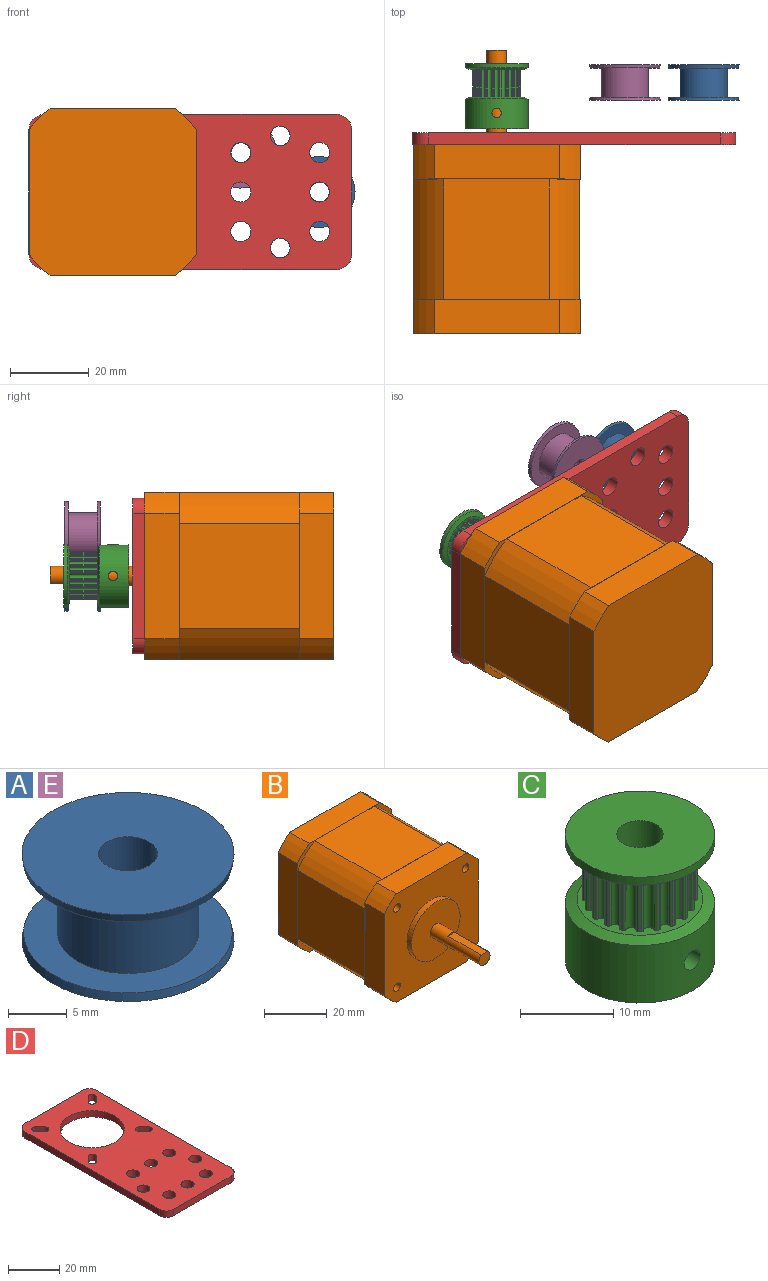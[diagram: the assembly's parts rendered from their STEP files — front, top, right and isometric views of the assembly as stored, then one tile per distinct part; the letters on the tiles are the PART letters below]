
ASSEMBLY  parts=5 mates=6
PART A: 8 faces, bbox 18x18x9 mm
  f0: plane 17.72x17.72mm, normal (0,0,-1), area 133.5mm2, adj f1,f6
  f1: cylinder r=6mm len=12mm, axis (0,0,-1), area 279mm2, adj f0,f2
  f2: plane 17.72x17.72mm, normal (0,0,1), area 133.5mm2, adj f1,f3
  f3: cone r=9mm half-angle=10deg, axis (0,0,-1), area 45.6mm2, adj f2,f4
  f4: plane 18x18mm, normal (0,0,-1), area 234.8mm2, adj f3,f7
  f5: plane 18x18mm, normal (0,0,1), area 234.8mm2, adj f6,f7
  f6: cone r=8.86mm half-angle=10deg, axis (0,0,1), area 45.6mm2, adj f0,f5
  f7: cylinder r=2.5mm len=9mm, axis (0,0,1), area 141.4mm2, adj f4,f5
PART B: 50 faces, bbox 42.4x72x42.4 mm
  f0: cylinder r=2.5mm len=22mm, axis (0,1,0), area 297.3mm2, adj f1,f2,f29,f30
  f1: plane 5x4.5mm, normal (0,-1,0), area 18.6mm2, adj f0,f29
  f2: plane 22x22mm, normal (0,-1,0), area 360.5mm2, adj f0,f3
  f3: cylinder r=11mm len=22mm, axis (0,1,0), area 138.2mm2, adj f2,f8
  f4: plane 31.78x8.75mm, normal (1,0,0), area 278mm2, adj f8,f9,f10,f32
  f5: plane 31.78x8.75mm, normal (0,0,-1), area 278mm2, adj f8,f9,f11,f32
  f6: plane 31.78x8.75mm, normal (-1,0,0), area 278mm2, adj f8,f11,f12,f32
  f7: plane 31.78x8.75mm, normal (0,0,1), area 278mm2, adj f8,f10,f12,f32
  f8: plane 42.42x42.42mm, normal (0,-1,0), area 1339.6mm2, adj f3,f4,f5,f6,f7,f9,f10,f11
  f9: cylinder r=26.5mm len=8.75mm, axis (0,1,0), area 66.1mm2, adj f4,f5,f8,f32
  f10: cylinder r=26.5mm len=8.75mm, axis (0,1,0), area 66.1mm2, adj f4,f7,f8,f32
  f11: cylinder r=26.5mm len=8.75mm, axis (0,1,0), area 66.1mm2, adj f5,f6,f8,f32
  f12: cylinder r=26.5mm len=8.75mm, axis (0,1,0), area 66.1mm2, adj f6,f7,f8,f32
  f13: cone r=1.25mm half-angle=59deg, axis (0,-1,0), area 5.7mm2, adj f14
  f14: cylinder r=1.25mm len=2.5mm, axis (0,-1,0), area 11.8mm2, adj f13,f15
  f15: plane 3x3mm, normal (0,-1,0), area 2.2mm2, adj f14,f16
  f16: cylinder r=1.5mm len=6mm, axis (0,-1,0), area 56.5mm2, adj f8,f15
  f17: cone r=1.25mm half-angle=59deg, axis (0,-1,0), area 5.7mm2, adj f18
  f18: cylinder r=1.25mm len=2.5mm, axis (0,-1,0), area 11.8mm2, adj f17,f19
  f19: plane 3x3mm, normal (0,-1,0), area 2.2mm2, adj f18,f20
  f20: cylinder r=1.5mm len=6mm, axis (0,-1,0), area 56.5mm2, adj f8,f19
  f21: cone r=1.25mm half-angle=59deg, axis (0,-1,0), area 5.7mm2, adj f22
  f22: cylinder r=1.25mm len=2.5mm, axis (0,-1,0), area 11.8mm2, adj f21,f23
  f23: plane 3x3mm, normal (0,-1,0), area 2.2mm2, adj f22,f24
  f24: cylinder r=1.5mm len=6mm, axis (0,-1,0), area 56.5mm2, adj f8,f23
  f25: cone r=1.25mm half-angle=59deg, axis (0,-1,0), area 5.7mm2, adj f26
  f26: cylinder r=1.25mm len=2.5mm, axis (0,-1,0), area 11.8mm2, adj f25,f27
  f27: plane 3x3mm, normal (0,-1,0), area 2.2mm2, adj f26,f28
  f28: cylinder r=1.5mm len=6mm, axis (0,-1,0), area 56.5mm2, adj f8,f27
  f29: plane 15x3mm, normal (0,0,1), area 45mm2, adj f0,f1,f30
  f30: plane 3x0.5mm, normal (0,-1,0), area 1mm2, adj f0,f29
  f31: plane 42.42x42.42mm, normal (0,-1,0), area 67.2mm2, adj f33,f34,f35,f36,f37,f38,f39,f40
  f32: plane 42.42x42.42mm, normal (0,1,0), area 67.2mm2, adj f4,f5,f6,f7,f9,f10,f11,f12
  f33: cylinder r=25mm len=30.5mm, axis (0,-1,0), area 335.5mm2, adj f31,f32,f34,f40
  f34: plane 30.5x26.79mm, normal (0,0,1), area 817.1mm2, adj f31,f32,f33,f35
  f35: cylinder r=25mm len=30.5mm, axis (0,-1,0), area 335.5mm2, adj f31,f32,f34,f36
  f36: plane 30.5x26.79mm, normal (1,0,0), area 817.1mm2, adj f31,f32,f35,f37
  f37: cylinder r=25mm len=30.5mm, axis (0,-1,0), area 335.5mm2, adj f31,f32,f36,f38
  f38: plane 30.5x26.79mm, normal (0,0,-1), area 817.1mm2, adj f31,f32,f37,f39
  f39: cylinder r=25mm len=30.5mm, axis (0,-1,0), area 335.5mm2, adj f31,f32,f38,f40
  f40: plane 30.5x26.79mm, normal (-1,0,0), area 817.1mm2, adj f31,f32,f33,f39
  f41: plane 42.42x42.42mm, normal (0,1,0), area 1748.1mm2, adj f42,f43,f44,f45,f46,f47,f48,f49
  f42: cylinder r=26.5mm len=8.75mm, axis (0,1,0), area 66.1mm2, adj f31,f41,f48,f49
  f43: cylinder r=26.5mm len=8.75mm, axis (0,1,0), area 66.1mm2, adj f31,f41,f47,f48
  f44: cylinder r=26.5mm len=8.75mm, axis (0,1,0), area 66.1mm2, adj f31,f41,f46,f47
  f45: cylinder r=26.5mm len=8.75mm, axis (0,1,0), area 66.1mm2, adj f31,f41,f46,f49
  f46: plane 31.78x8.75mm, normal (0,0,1), area 278mm2, adj f31,f41,f44,f45
  f47: plane 31.78x8.75mm, normal (-1,0,0), area 278mm2, adj f31,f41,f43,f44
  f48: plane 31.78x8.75mm, normal (0,0,-1), area 278mm2, adj f31,f41,f42,f43
  f49: plane 31.78x8.75mm, normal (1,0,0), area 278mm2, adj f31,f41,f42,f45
PART C: 131 faces, bbox 16x16x16.5 mm
  f0: cylinder r=8mm len=16mm, axis (0,0,-1), area 370mm2, adj f123,f124,f129,f130
  f1: cylinder r=2.5mm len=16.5mm, axis (0,0,-1), area 249.8mm2, adj f123,f126,f129,f130
  f2: cylinder r=6.11mm len=7mm, axis (0,0,-1), area 2.2mm2, adj f3,f14,f122,f125
  f3: cylinder r=0.19mm len=7mm, axis (0,0,-1), area 1.8mm2, adj f2,f4,f122,f125
  f4: cylinder r=5mm len=7mm, axis (0,0,-1), area 1.6mm2, adj f3,f5,f122,f125
  f5: cylinder r=0.56mm len=7mm, axis (0,0,-1), area 9.4mm2, adj f4,f6,f122,f125
  f6: cylinder r=5mm len=7mm, axis (0,0,-1), area 1.6mm2, adj f5,f7,f122,f125
  f7: cylinder r=0.19mm len=7mm, axis (0,0,-1), area 1.8mm2, adj f6,f8,f122,f125
  f8: cylinder r=6.11mm len=7mm, axis (0,0,-1), area 2.2mm2, adj f7,f117,f122,f125
  f9: cylinder r=6.11mm len=7mm, axis (0,0,-1), area 2.2mm2, adj f10,f20,f122,f125
  f10: cylinder r=0.19mm len=7mm, axis (0,0,-1), area 1.8mm2, adj f9,f11,f122,f125
  f11: cylinder r=5mm len=7mm, axis (0,0,-1), area 1.6mm2, adj f10,f12,f122,f125
  f12: cylinder r=0.56mm len=7mm, axis (0,0,-1), area 9.4mm2, adj f11,f13,f122,f125
  f13: cylinder r=5mm len=7mm, axis (0,0,-1), area 1.6mm2, adj f12,f14,f122,f125
  f14: cylinder r=0.19mm len=7mm, axis (0,0,-1), area 1.8mm2, adj f2,f13,f122,f125
  f15: cylinder r=6.11mm len=7mm, axis (0,0,-1), area 2.2mm2, adj f16,f26,f122,f125
  f16: cylinder r=0.19mm len=7mm, axis (0,0,-1), area 1.8mm2, adj f15,f17,f122,f125
  f17: cylinder r=5mm len=7mm, axis (0,0,-1), area 1.6mm2, adj f16,f18,f122,f125
  f18: cylinder r=0.56mm len=7mm, axis (0,0,-1), area 9.4mm2, adj f17,f19,f122,f125
  f19: cylinder r=5mm len=7mm, axis (0,0,-1), area 1.6mm2, adj f18,f20,f122,f125
  f20: cylinder r=0.19mm len=7mm, axis (0,0,-1), area 1.8mm2, adj f9,f19,f122,f125
  f21: cylinder r=6.11mm len=7mm, axis (0,0,-1), area 2.2mm2, adj f22,f32,f122,f125
  f22: cylinder r=0.19mm len=7mm, axis (0,0,-1), area 1.8mm2, adj f21,f23,f122,f125
  f23: cylinder r=5mm len=7mm, axis (0,0,-1), area 1.6mm2, adj f22,f24,f122,f125
  f24: cylinder r=0.56mm len=7mm, axis (0,0,-1), area 9.4mm2, adj f23,f25,f122,f125
  f25: cylinder r=5mm len=7mm, axis (0,0,-1), area 1.6mm2, adj f24,f26,f122,f125
  f26: cylinder r=0.19mm len=7mm, axis (0,0,-1), area 1.8mm2, adj f15,f25,f122,f125
  f27: cylinder r=6.11mm len=7mm, axis (0,0,-1), area 2.2mm2, adj f28,f38,f122,f125
  f28: cylinder r=0.19mm len=7mm, axis (0,0,-1), area 1.8mm2, adj f27,f29,f122,f125
  f29: cylinder r=5mm len=7mm, axis (0,0,-1), area 1.6mm2, adj f28,f30,f122,f125
  f30: cylinder r=0.56mm len=7mm, axis (0,0,-1), area 9.4mm2, adj f29,f31,f122,f125
  f31: cylinder r=5mm len=7mm, axis (0,0,-1), area 1.6mm2, adj f30,f32,f122,f125
  f32: cylinder r=0.19mm len=7mm, axis (0,0,-1), area 1.8mm2, adj f21,f31,f122,f125
  f33: cylinder r=6.11mm len=7mm, axis (0,0,-1), area 2.2mm2, adj f34,f44,f122,f125
  f34: cylinder r=0.19mm len=7mm, axis (0,0,-1), area 1.8mm2, adj f33,f35,f122,f125
  f35: cylinder r=5mm len=7mm, axis (0,0,-1), area 1.6mm2, adj f34,f36,f122,f125
  f36: cylinder r=0.56mm len=7mm, axis (0,0,-1), area 9.4mm2, adj f35,f37,f122,f125
  f37: cylinder r=5mm len=7mm, axis (0,0,-1), area 1.6mm2, adj f36,f38,f122,f125
  f38: cylinder r=0.19mm len=7mm, axis (0,0,-1), area 1.8mm2, adj f27,f37,f122,f125
  f39: cylinder r=6.11mm len=7mm, axis (0,0,-1), area 2.2mm2, adj f40,f50,f122,f125
  f40: cylinder r=0.19mm len=7mm, axis (0,0,-1), area 1.8mm2, adj f39,f41,f122,f125
  f41: cylinder r=5mm len=7mm, axis (0,0,-1), area 1.6mm2, adj f40,f42,f122,f125
  f42: cylinder r=0.56mm len=7mm, axis (0,0,-1), area 9.4mm2, adj f41,f43,f122,f125
  f43: cylinder r=5mm len=7mm, axis (0,0,-1), area 1.6mm2, adj f42,f44,f122,f125
  f44: cylinder r=0.19mm len=7mm, axis (0,0,-1), area 1.8mm2, adj f33,f43,f122,f125
  f45: cylinder r=6.11mm len=7mm, axis (0,0,-1), area 2.2mm2, adj f46,f56,f122,f125
  f46: cylinder r=0.19mm len=7mm, axis (0,0,-1), area 1.8mm2, adj f45,f47,f122,f125
  f47: cylinder r=5mm len=7mm, axis (0,0,-1), area 1.6mm2, adj f46,f48,f122,f125
  f48: cylinder r=0.56mm len=7mm, axis (0,0,-1), area 9.4mm2, adj f47,f49,f122,f125
  f49: cylinder r=5mm len=7mm, axis (0,0,-1), area 1.6mm2, adj f48,f50,f122,f125
  f50: cylinder r=0.19mm len=7mm, axis (0,0,-1), area 1.8mm2, adj f39,f49,f122,f125
  f51: cylinder r=6.11mm len=7mm, axis (0,0,-1), area 2.2mm2, adj f52,f62,f122,f125
  f52: cylinder r=0.19mm len=7mm, axis (0,0,-1), area 1.8mm2, adj f51,f53,f122,f125
  f53: cylinder r=5mm len=7mm, axis (0,0,-1), area 1.6mm2, adj f52,f54,f122,f125
  f54: cylinder r=0.56mm len=7mm, axis (0,0,-1), area 9.4mm2, adj f53,f55,f122,f125
  f55: cylinder r=5mm len=7mm, axis (0,0,-1), area 1.6mm2, adj f54,f56,f122,f125
  f56: cylinder r=0.19mm len=7mm, axis (0,0,-1), area 1.8mm2, adj f45,f55,f122,f125
  f57: cylinder r=6.11mm len=7mm, axis (0,0,-1), area 2.2mm2, adj f58,f68,f122,f125
  f58: cylinder r=0.19mm len=7mm, axis (0,0,-1), area 1.8mm2, adj f57,f59,f122,f125
  f59: cylinder r=5mm len=7mm, axis (0,0,-1), area 1.6mm2, adj f58,f60,f122,f125
  f60: cylinder r=0.56mm len=7mm, axis (0,0,-1), area 9.4mm2, adj f59,f61,f122,f125
  f61: cylinder r=5mm len=7mm, axis (0,0,-1), area 1.6mm2, adj f60,f62,f122,f125
  f62: cylinder r=0.19mm len=7mm, axis (0,0,-1), area 1.8mm2, adj f51,f61,f122,f125
  f63: cylinder r=6.11mm len=7mm, axis (0,0,-1), area 2.2mm2, adj f64,f74,f122,f125
  f64: cylinder r=0.19mm len=7mm, axis (0,0,-1), area 1.8mm2, adj f63,f65,f122,f125
  f65: cylinder r=5mm len=7mm, axis (0,0,-1), area 1.6mm2, adj f64,f66,f122,f125
  f66: cylinder r=0.56mm len=7mm, axis (0,0,-1), area 9.4mm2, adj f65,f67,f122,f125
  f67: cylinder r=5mm len=7mm, axis (0,0,-1), area 1.6mm2, adj f66,f68,f122,f125
  f68: cylinder r=0.19mm len=7mm, axis (0,0,-1), area 1.8mm2, adj f57,f67,f122,f125
  f69: cylinder r=6.11mm len=7mm, axis (0,0,-1), area 2.2mm2, adj f70,f80,f122,f125
  f70: cylinder r=0.19mm len=7mm, axis (0,0,-1), area 1.8mm2, adj f69,f71,f122,f125
  f71: cylinder r=5mm len=7mm, axis (0,0,-1), area 1.6mm2, adj f70,f72,f122,f125
  f72: cylinder r=0.56mm len=7mm, axis (0,0,-1), area 9.4mm2, adj f71,f73,f122,f125
  f73: cylinder r=5mm len=7mm, axis (0,0,-1), area 1.6mm2, adj f72,f74,f122,f125
  f74: cylinder r=0.19mm len=7mm, axis (0,0,-1), area 1.8mm2, adj f63,f73,f122,f125
  f75: cylinder r=6.11mm len=7mm, axis (0,0,-1), area 2.2mm2, adj f76,f86,f122,f125
  f76: cylinder r=0.19mm len=7mm, axis (0,0,-1), area 1.8mm2, adj f75,f77,f122,f125
  f77: cylinder r=5mm len=7mm, axis (0,0,-1), area 1.6mm2, adj f76,f78,f122,f125
  f78: cylinder r=0.56mm len=7mm, axis (0,0,-1), area 9.4mm2, adj f77,f79,f122,f125
  f79: cylinder r=5mm len=7mm, axis (0,0,-1), area 1.6mm2, adj f78,f80,f122,f125
  f80: cylinder r=0.19mm len=7mm, axis (0,0,-1), area 1.8mm2, adj f69,f79,f122,f125
  f81: cylinder r=6.11mm len=7mm, axis (0,0,-1), area 2.2mm2, adj f82,f92,f122,f125
  f82: cylinder r=0.19mm len=7mm, axis (0,0,-1), area 1.8mm2, adj f81,f83,f122,f125
  f83: cylinder r=5mm len=7mm, axis (0,0,-1), area 1.6mm2, adj f82,f84,f122,f125
  f84: cylinder r=0.56mm len=7mm, axis (0,0,-1), area 9.4mm2, adj f83,f85,f122,f125
  f85: cylinder r=5mm len=7mm, axis (0,0,-1), area 1.6mm2, adj f84,f86,f122,f125
  f86: cylinder r=0.19mm len=7mm, axis (0,0,-1), area 1.8mm2, adj f75,f85,f122,f125
  f87: cylinder r=6.11mm len=7mm, axis (0,0,-1), area 2.2mm2, adj f88,f98,f122,f125
  f88: cylinder r=0.19mm len=7mm, axis (0,0,-1), area 1.8mm2, adj f87,f89,f122,f125
  f89: cylinder r=5mm len=7mm, axis (0,0,-1), area 1.6mm2, adj f88,f90,f122,f125
  f90: cylinder r=0.56mm len=7mm, axis (0,0,-1), area 9.4mm2, adj f89,f91,f122,f125
  f91: cylinder r=5mm len=7mm, axis (0,0,-1), area 1.6mm2, adj f90,f92,f122,f125
  f92: cylinder r=0.19mm len=7mm, axis (0,0,-1), area 1.8mm2, adj f81,f91,f122,f125
  f93: cylinder r=6.11mm len=7mm, axis (0,0,-1), area 2.2mm2, adj f94,f104,f122,f125
  f94: cylinder r=0.19mm len=7mm, axis (0,0,-1), area 1.8mm2, adj f93,f95,f122,f125
  f95: cylinder r=5mm len=7mm, axis (0,0,-1), area 1.6mm2, adj f94,f96,f122,f125
  f96: cylinder r=0.56mm len=7mm, axis (0,0,-1), area 9.4mm2, adj f95,f97,f122,f125
  f97: cylinder r=5mm len=7mm, axis (0,0,-1), area 1.6mm2, adj f96,f98,f122,f125
  f98: cylinder r=0.19mm len=7mm, axis (0,0,-1), area 1.8mm2, adj f87,f97,f122,f125
  f99: cylinder r=6.11mm len=7mm, axis (0,0,-1), area 2.2mm2, adj f100,f110,f122,f125
  f100: cylinder r=0.19mm len=7mm, axis (0,0,-1), area 1.8mm2, adj f99,f101,f122,f125
  f101: cylinder r=5mm len=7mm, axis (0,0,-1), area 1.6mm2, adj f100,f102,f122,f125
  f102: cylinder r=0.56mm len=7mm, axis (0,0,-1), area 9.4mm2, adj f101,f103,f122,f125
  f103: cylinder r=5mm len=7mm, axis (0,0,-1), area 1.6mm2, adj f102,f104,f122,f125
  f104: cylinder r=0.19mm len=7mm, axis (0,0,-1), area 1.8mm2, adj f93,f103,f122,f125
  f105: cylinder r=6.11mm len=7mm, axis (0,0,-1), area 2.2mm2, adj f106,f116,f122,f125
  f106: cylinder r=0.19mm len=7mm, axis (0,0,-1), area 1.8mm2, adj f105,f107,f122,f125
  f107: cylinder r=5mm len=7mm, axis (0,0,-1), area 1.6mm2, adj f106,f108,f122,f125
  f108: cylinder r=0.56mm len=7mm, axis (0,0,-1), area 9.4mm2, adj f107,f109,f122,f125
  f109: cylinder r=5mm len=7mm, axis (0,0,-1), area 1.6mm2, adj f108,f110,f122,f125
  f110: cylinder r=0.19mm len=7mm, axis (0,0,-1), area 1.8mm2, adj f99,f109,f122,f125
  f111: cylinder r=6.11mm len=7mm, axis (0,0,-1), area 2.2mm2, adj f112,f121,f122,f125
  f112: cylinder r=0.19mm len=7mm, axis (0,0,-1), area 1.8mm2, adj f111,f113,f122,f125
  f113: cylinder r=5mm len=7mm, axis (0,0,-1), area 1.6mm2, adj f112,f114,f122,f125
  f114: cylinder r=0.56mm len=7mm, axis (0,0,-1), area 9.4mm2, adj f113,f115,f122,f125
  f115: cylinder r=5mm len=7mm, axis (0,0,-1), area 1.6mm2, adj f114,f116,f122,f125
  f116: cylinder r=0.19mm len=7mm, axis (0,0,-1), area 1.8mm2, adj f105,f115,f122,f125
  f117: cylinder r=0.19mm len=7mm, axis (0,0,-1), area 1.8mm2, adj f8,f118,f122,f125
  f118: cylinder r=5mm len=7mm, axis (0,0,-1), area 1.6mm2, adj f117,f119,f122,f125
  f119: cylinder r=0.56mm len=7mm, axis (0,0,-1), area 9.4mm2, adj f118,f120,f122,f125
  f120: cylinder r=5mm len=7mm, axis (0,0,-1), area 1.6mm2, adj f119,f121,f122,f125
  f121: cylinder r=0.19mm len=7mm, axis (0,0,-1), area 1.8mm2, adj f111,f120,f122,f125
  f122: plane 13.48x13.48mm, normal (0,0,1), area 40mm2, adj f2,f3,f4,f5,f6,f7,f8,f9
  f123: plane 16x16mm, normal (0,0,-1), area 181.4mm2, adj f0,f1
  f124: cone r=6.74mm half-angle=70deg, axis (0,0,-1), area 62mm2, adj f0,f122
  f125: plane 13.48x13.48mm, normal (0,0,-1), area 40mm2, adj f2,f3,f4,f5,f6,f7,f8,f9
  f126: plane 16x16mm, normal (0,0,1), area 181.4mm2, adj f1,f128
  f127: cone r=8mm half-angle=70deg, axis (0,0,1), area 62mm2, adj f125,f128
  f128: cylinder r=8mm len=16mm, axis (0,0,-1), area 52.4mm2, adj f126,f127
  f129: cylinder r=1.2mm len=5.81mm, axis (0,1,0), area 42.3mm2, adj f0,f1
  f130: cylinder r=1.2mm len=5.81mm, axis (-1,0,0), area 42.3mm2, adj f0,f1
PART D: 35 faces, bbox 39.5x82x3 mm
  f0: plane 82x39.5mm, normal (0,0,1), area 2498.5mm2, adj f2,f3,f4,f5,f6,f7,f8,f9
  f1: plane 82x39.5mm, normal (0,0,-1), area 2498.5mm2, adj f2,f3,f4,f5,f6,f7,f8,f9
  f2: cylinder r=4mm len=4mm, axis (0,0,-1), area 18.8mm2, adj f0,f1,f3,f9
  f3: plane 31.5x3mm, normal (0,-1,0), area 94.5mm2, adj f0,f1,f2,f4
  f4: cylinder r=4mm len=4mm, axis (0,0,-1), area 18.8mm2, adj f0,f1,f3,f5
  f5: plane 74x3mm, normal (1,0,0), area 222mm2, adj f0,f1,f4,f6
  f6: cylinder r=4mm len=4mm, axis (0,0,-1), area 18.8mm2, adj f0,f1,f5,f7
  f7: plane 31.5x3mm, normal (0,1,0), area 94.5mm2, adj f0,f1,f6,f8
  f8: cylinder r=4mm len=4mm, axis (0,0,-1), area 18.8mm2, adj f0,f1,f7,f9
  f9: plane 74x3mm, normal (-1,0,0), area 222mm2, adj f0,f1,f2,f8
  f10: cylinder r=12.5mm len=25mm, axis (0,0,-1), area 235.6mm2, adj f0,f1
  f11: cylinder r=1.55mm len=3mm, axis (0,0,-1), area 14.6mm2, adj f0,f1,f12,f14
  f12: plane 3x2.5mm, normal (-0.71,0.71,0), area 10.6mm2, adj f0,f1,f11,f13
  f13: cylinder r=1.55mm len=3mm, axis (0,0,-1), area 14.6mm2, adj f0,f1,f12,f14
  f14: plane 3x2.5mm, normal (0.71,-0.71,0), area 10.6mm2, adj f0,f1,f11,f13
  f15: cylinder r=2.55mm len=5.1mm, axis (0,0,-1), area 48.1mm2, adj f0,f1
  f16: cylinder r=2.55mm len=5.1mm, axis (0,0,-1), area 48.1mm2, adj f0,f1
  f17: cylinder r=2.55mm len=5.1mm, axis (0,0,-1), area 48.1mm2, adj f0,f1
  f18: cylinder r=2.55mm len=5.1mm, axis (0,0,-1), area 48.1mm2, adj f0,f1
  f19: cylinder r=2.55mm len=5.1mm, axis (0,0,-1), area 48.1mm2, adj f0,f1
  f20: cylinder r=2.55mm len=5.1mm, axis (0,0,-1), area 48.1mm2, adj f0,f1
  f21: cylinder r=1.55mm len=3mm, axis (0,0,-1), area 14.6mm2, adj f0,f1,f22,f24
  f22: plane 3x2.5mm, normal (-0.71,-0.71,0), area 10.6mm2, adj f0,f1,f21,f23
  f23: cylinder r=1.55mm len=3mm, axis (0,0,-1), area 14.6mm2, adj f0,f1,f22,f24
  f24: plane 3x2.5mm, normal (0.71,0.71,0), area 10.6mm2, adj f0,f1,f21,f23
  f25: cylinder r=1.55mm len=3mm, axis (0,0,-1), area 14.6mm2, adj f0,f1,f26,f28
  f26: plane 3x2.5mm, normal (0.71,-0.71,0), area 10.6mm2, adj f0,f1,f25,f27
  f27: cylinder r=1.55mm len=3mm, axis (0,0,-1), area 14.6mm2, adj f0,f1,f26,f28
  f28: plane 3x2.5mm, normal (-0.71,0.71,0), area 10.6mm2, adj f0,f1,f25,f27
  f29: cylinder r=1.55mm len=3mm, axis (0,0,-1), area 14.6mm2, adj f0,f1,f30,f32
  f30: plane 3x2.5mm, normal (0.71,0.71,0), area 10.6mm2, adj f0,f1,f29,f31
  f31: cylinder r=1.55mm len=3mm, axis (0,0,-1), area 14.6mm2, adj f0,f1,f30,f32
  f32: plane 3x2.5mm, normal (-0.71,-0.71,0), area 10.6mm2, adj f0,f1,f29,f31
  f33: cylinder r=2.5mm len=5mm, axis (0,0,1), area 47.1mm2, adj f0,f1
  f34: cylinder r=2.5mm len=5mm, axis (0,0,1), area 47.1mm2, adj f0,f1
PART E: same geometry as A
PLACE A rot(axis=(0,-0.71,0.71),180deg) t=(692.73,-901.87,59.25)mm
PLACE B rot(axis=(1,0,0),180deg) t=(640.18,-924.81,59.25)mm
PLACE C rot(axis=(-0.58,-0.58,-0.58),120deg) t=(640.18,-909.26,59.25)mm
PLACE D rot(axis=(0.58,-0.58,0.58),120deg) t=(640.18,-921.81,59.25)mm
PLACE E rot(axis=(0,-0.71,0.71),180deg) t=(672.73,-901.87,69.25)mm
MATE slider A.f1 <-> D.f17  axis (0,-1,0) through (692.73,-913.56,59.25)mm
MATE slider C.f0 <-> B.f0  axis (0,1,0) through (640.18,-904.26,59.25)mm
MATE slider E.f1 <-> D.f16  axis (0,-1,0) through (672.73,-913.56,69.25)mm
MATE fastened B.f0 <-> D.f10  axis (0,1,0) through (640.18,-924.81,59.25)mm
MATE planar E.f1 <-> A.f1  axis (0,1,0) through (672.73,-912.76,69.25)mm
MATE planar C.f78 <-> E.f1  axis (0,1,0) through (635.39,-912.76,55.77)mm
